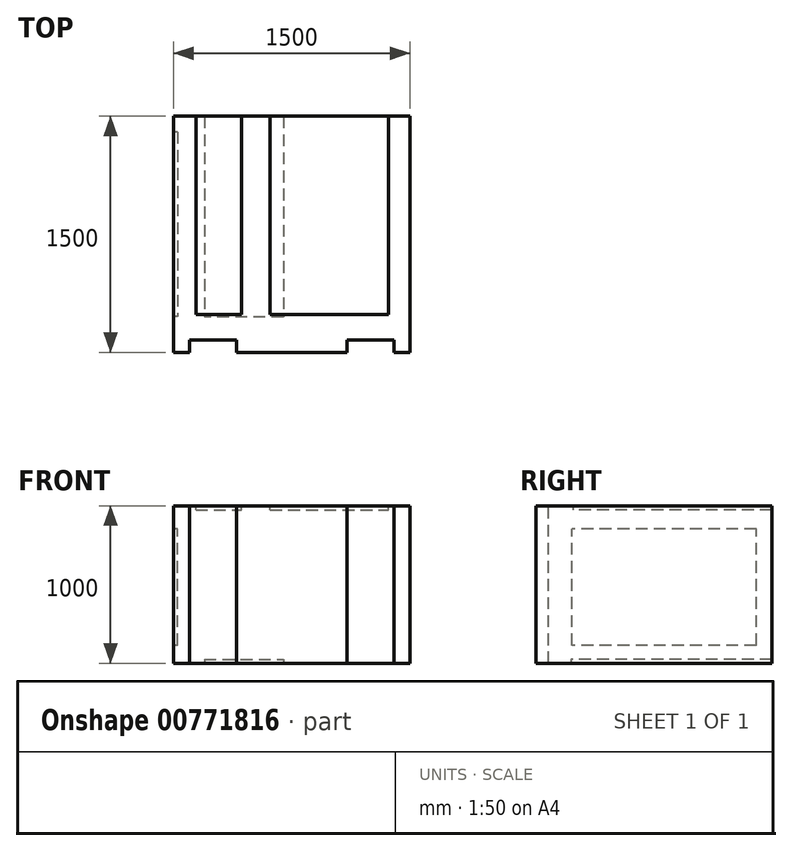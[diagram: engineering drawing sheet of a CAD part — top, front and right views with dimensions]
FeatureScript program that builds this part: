
annotation { "Feature Type Name" : "Feature", "Feature Type Description" : "" }
export const myFeature = defineFeature(function(context is Context, id is Id, definition is map)
    precondition{}
    {
        {
            var Q0;
            Q0=qCreatedBy(makeId("Front.planeOp"),FACE);
            var sketch = newSketch(context, id + "F0", { "sketchPlane" : qUnion([Q0])});
            skLineSegment(sketch, "E0.bottom", {"start": v(0, 0) * mm, "end": v(1500, 0) * mm});
            skLineSegment(sketch, "E0.top", {"start": v(0, 1000) * mm, "end": v(1500, 1000) * mm});
            skLineSegment(sketch, "E0.left", {"start": v(0, 0) * mm, "end": v(0, 1000) * mm});
            skLineSegment(sketch, "E0.right", {"start": v(1500, 0) * mm, "end": v(1500, 1000) * mm});
            skSolve(sketch);
        }
        {
            var Q0;
            Q0=makeQuery(id+"F0.imprint","IMPRINT",FACE,{"disambiguationData":[TD([[makeQuery(id+"F0.imprint","IMPRINT",EDGE,{"derivedFrom":sQuery(id+"F0.wireOp",EDGE,"E0.bottom")}),1.0]])]});
            extrude(context, id + "F1", {"entities" : qUnion([Q0]), "depth" : 1500 * mm, "offsetDistance" : 25 * mm});
        }
        {
            var Q0;
            Q0=makeQuery(id+"F1.opExtrude","SWEPT_FACE",FACE,{"disambiguationData":[OSD([sQuery(id+"F0.wireOp",EDGE,"E0.top")])]});
            var sketch = newSketch(context, id + "F2", { "sketchPlane" : qUnion([Q0])});
            skLineSegment(sketch, "E1.bottom", {"start": v(100, -1500) * mm, "end": v(400, -1500) * mm});
            skLineSegment(sketch, "E1.top", {"start": v(100, -1420) * mm, "end": v(400, -1420) * mm});
            skLineSegment(sketch, "E1.left", {"start": v(100, -1500) * mm, "end": v(100, -1420) * mm});
            skLineSegment(sketch, "E1.right", {"start": v(400, -1500) * mm, "end": v(400, -1420) * mm});
            skLineSegment(sketch, "E2.1.0.0", {"start": v(1100, -1500) * mm, "end": v(1400, -1500) * mm});
            skLineSegment(sketch, "E2.1.0.1", {"start": v(1100, -1420) * mm, "end": v(1400, -1420) * mm});
            skLineSegment(sketch, "E2.1.0.2", {"start": v(1100, -1500) * mm, "end": v(1100, -1420) * mm});
            skLineSegment(sketch, "E2.1.0.3", {"start": v(1400, -1500) * mm, "end": v(1400, -1420) * mm});
            skLineSegment(sketch, "E2.direction1", {"start": v(100, -1500) * mm, "end": v(1100, -1500) * mm, "construction": true});
            skSolve(sketch);
        }
        {
            var Q0;
            Q0 = qSketchRegion(id + "F2", true);
            extrude(context, id + "F3", {"entities" : qUnion([Q0]), "operationType" : NewBodyOperationType.REMOVE, "oppositeDirection" : true, "depth" : 1000 * mm, "offsetDistance" : 25 * mm});
        }
        {
            var Q0;
            Q0=makeQuery(id+"F1.opExtrude","SWEPT_FACE",FACE,{"disambiguationData":[OSD([sQuery(id+"F0.wireOp",EDGE,"E0.top")])]});
            var sketch = newSketch(context, id + "F4", { "sketchPlane" : qUnion([Q0])});
            skLineSegment(sketch, "E3.bottom", {"start": v(140.85, 0) * mm, "end": v(431.65, 0) * mm});
            skLineSegment(sketch, "E3.top", {"start": v(140.85, -1259.66) * mm, "end": v(431.65, -1259.66) * mm});
            skLineSegment(sketch, "E3.left", {"start": v(140.85, 0) * mm, "end": v(140.85, -1259.66) * mm});
            skLineSegment(sketch, "E3.right", {"start": v(431.65, 0) * mm, "end": v(431.65, -1259.66) * mm});
            skLineSegment(sketch, "E4.bottom", {"start": v(612.25, 0) * mm, "end": v(1365.27, 0) * mm});
            skLineSegment(sketch, "E4.top", {"start": v(612.25, -1259.66) * mm, "end": v(1365.27, -1259.66) * mm});
            skLineSegment(sketch, "E4.left", {"start": v(612.25, 0) * mm, "end": v(612.25, -1259.66) * mm});
            skLineSegment(sketch, "E4.right", {"start": v(1365.27, 0) * mm, "end": v(1365.27, -1259.66) * mm});
            skSolve(sketch);
        }
        {
            var Q0;
            Q0=makeQuery(id+"F4.imprint","IMPRINT",FACE,{"disambiguationData":[TD([[makeQuery(id+"F4.imprint","IMPRINT",EDGE,{"derivedFrom":sQuery(id+"F4.wireOp",EDGE,"E3.bottom")}),-1.0]])]});
            var Q1;
            Q1=makeQuery(id+"F4.imprint","IMPRINT",FACE,{"disambiguationData":[TD([[makeQuery(id+"F4.imprint","IMPRINT",EDGE,{"derivedFrom":sQuery(id+"F4.wireOp",EDGE,"E4.bottom")}),-1.0]])]});
            extrude(context, id + "F5", {"entities" : qUnion([Q0, Q1]), "operationType" : NewBodyOperationType.REMOVE, "oppositeDirection" : true, "depth" : 25 * mm, "offsetDistance" : 25 * mm});
        }
        {
            var Q0;
            Q0=makeQuery(id+"F1.opExtrude","SWEPT_FACE",FACE,{"disambiguationData":[OSD([sQuery(id+"F0.wireOp",EDGE,"E0.left")])]});
            var sketch = newSketch(context, id + "F6", { "sketchPlane" : qUnion([Q0])});
            skLineSegment(sketch, "E5.bottom", {"start": v(99.89, 115.13) * mm, "end": v(1270.84, 115.13) * mm});
            skLineSegment(sketch, "E5.top", {"start": v(99.89, 852.72) * mm, "end": v(1270.84, 852.72) * mm});
            skLineSegment(sketch, "E5.left", {"start": v(99.89, 115.13) * mm, "end": v(99.89, 852.72) * mm});
            skLineSegment(sketch, "E5.right", {"start": v(1270.84, 115.13) * mm, "end": v(1270.84, 852.72) * mm});
            skSolve(sketch);
        }
        {
            var Q0;
            Q0=makeQuery(id+"F6.imprint","IMPRINT",FACE,{"disambiguationData":[TD([[makeQuery(id+"F6.imprint","IMPRINT",EDGE,{"derivedFrom":sQuery(id+"F6.wireOp",EDGE,"E5.bottom")}),1.0]])]});
            extrude(context, id + "F7", {"entities" : qUnion([Q0]), "operationType" : NewBodyOperationType.REMOVE, "oppositeDirection" : true, "depth" : 25 * mm, "offsetDistance" : 25 * mm});
        }
        {
            var Q0;
            Q0=makeQuery(id+"F1.opExtrude","SWEPT_FACE",FACE,{"disambiguationData":[OSD([sQuery(id+"F0.wireOp",EDGE,"E0.bottom")])]});
            var sketch = newSketch(context, id + "F8", { "sketchPlane" : qUnion([Q0])});
            skLineSegment(sketch, "E6.bottom", {"start": v(696.79, 0) * mm, "end": v(195.75, 0) * mm});
            skLineSegment(sketch, "E6.top", {"start": v(696.79, 1276.9) * mm, "end": v(195.75, 1276.9) * mm});
            skLineSegment(sketch, "E6.left", {"start": v(696.79, 0) * mm, "end": v(696.79, 1276.9) * mm});
            skLineSegment(sketch, "E6.right", {"start": v(195.75, 0) * mm, "end": v(195.75, 1276.9) * mm});
            skSolve(sketch);
        }
        {
            var Q0;
            Q0=makeQuery(id+"F8.imprint","IMPRINT",FACE,{"disambiguationData":[TD([[makeQuery(id+"F8.imprint","IMPRINT",EDGE,{"derivedFrom":sQuery(id+"F8.wireOp",EDGE,"E6.bottom")}),1.0]])]});
            extrude(context, id + "F9", {"entities" : qUnion([Q0]), "operationType" : NewBodyOperationType.REMOVE, "oppositeDirection" : true, "depth" : 25 * mm, "offsetDistance" : 25 * mm});
        }
    });
